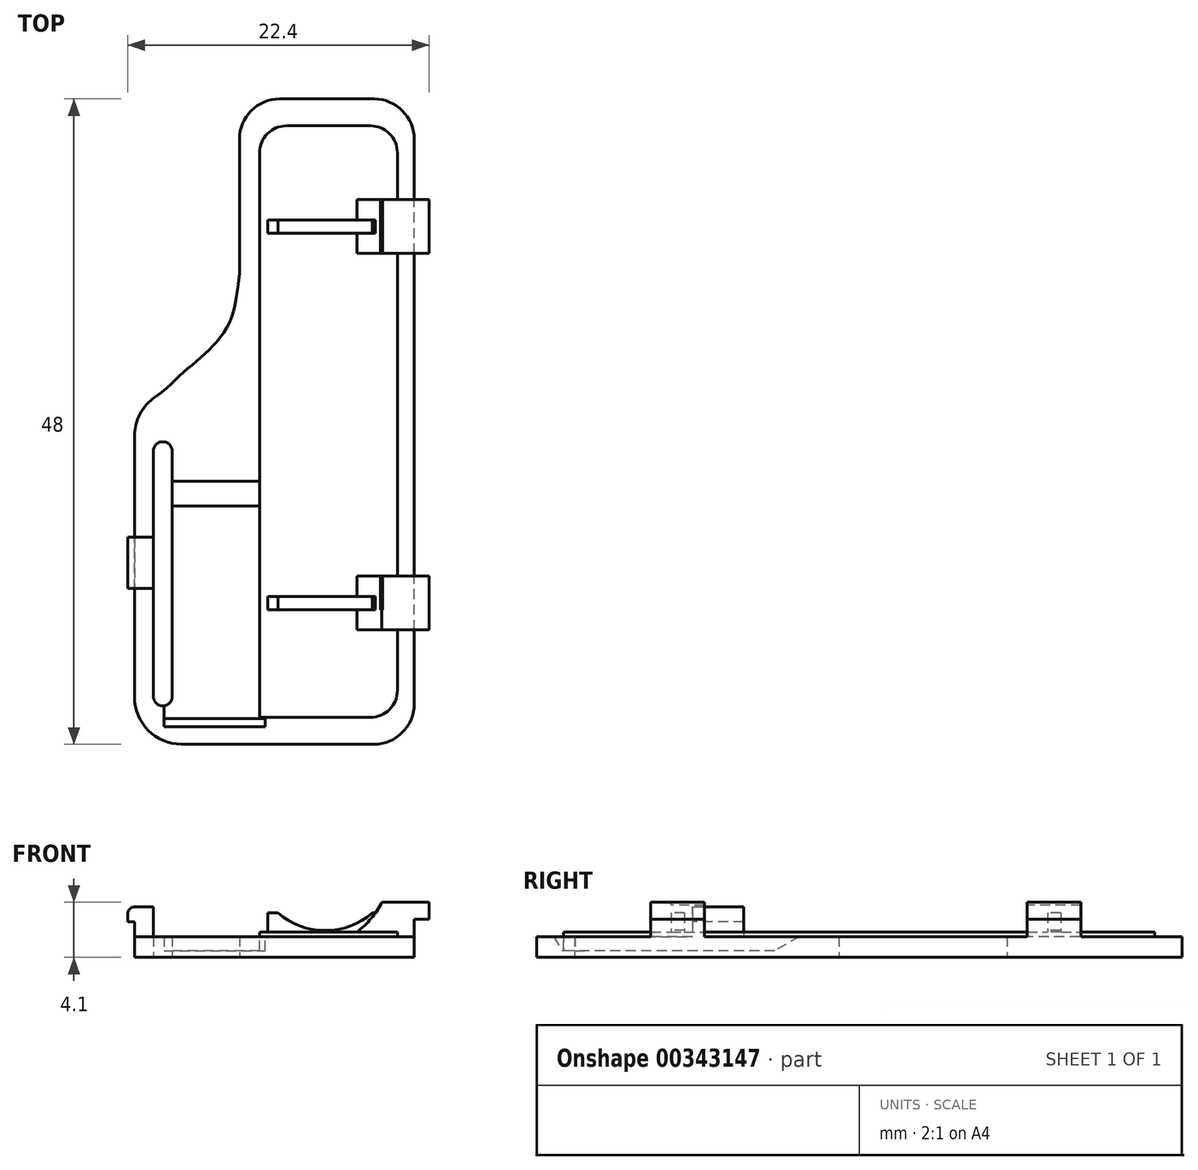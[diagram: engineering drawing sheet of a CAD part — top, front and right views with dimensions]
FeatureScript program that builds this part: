
annotation { "Feature Type Name" : "Feature", "Feature Type Description" : "" }
export const myFeature = defineFeature(function(context is Context, id is Id, definition is map)
    precondition{}
    {
        {
            var Q0;
            Q0=qCreatedBy(makeId("Top.planeOp"),FACE);
            var sketch = newSketch(context, id + "F0", { "sketchPlane" : qUnion([Q0])});
            skLineSegment(sketch, "E0.bottom", {"start": v(1.82, -24.92) * mm, "end": v(-12.48, -24.92) * mm});
            skLineSegment(sketch, "E0.top", {"start": v(1.82, 23.08) * mm, "end": v(-5.18, 23.08) * mm});
            skLineSegment(sketch, "E0.left", {"start": v(4.82, -21.92) * mm, "end": v(4.82, 20.08) * mm});
            skLineSegment(sketch, "E0.right", {"start": v(-15.98, -21.42) * mm, "end": v(-15.98, -2) * mm});
            skLineSegment(sketch, "E1", {"start": v(-8.18, 20.08) * mm, "end": v(-8.18, 10.08) * mm});
            skPoint(sketch, "E2.visualSharp", {"position": v(4.82, 23.08) * mm});
            skArc(sketch, "E2.filletArc", {"start": v(4.82, 20.08) * mm, "mid": v(3.94, 22.2) * mm, "end": v(1.82, 23.08) * mm});
            skPoint(sketch, "E3.visualSharp", {"position": v(4.82, -24.92) * mm});
            skArc(sketch, "E3.filletArc", {"start": v(1.82, -24.92) * mm, "mid": v(3.94, -24.04) * mm, "end": v(4.82, -21.92) * mm});
            skPoint(sketch, "E4.visualSharp", {"position": v(-15.98, -24.92) * mm});
            skArc(sketch, "E4.filletArc", {"start": v(-15.98, -21.42) * mm, "mid": v(-14.95, -23.9) * mm, "end": v(-12.48, -24.92) * mm});
            skPoint(sketch, "E5.visualSharp", {"position": v(-8.18, 23.08) * mm});
            skArc(sketch, "E5.filletArc", {"start": v(-5.18, 23.08) * mm, "mid": v(-7.3, 22.2) * mm, "end": v(-8.18, 20.08) * mm});
            skFitSpline(sketch, "E6", {"points": [v(-8.18, 10.08) * mm, v(-9.53, 5.44) * mm, v(-11.08, 3.82) * mm, v(-12.77, 2.37) * mm, v(-15.98, 0.08) * mm], "startDerivative": vector(-2.45, -27.24) * mm, "endDerivative": vector(-20.78, -9.12) * mm});
            skArc(sketch, "E7.filletArc", {"start": v(-14.43, 0.92) * mm, "mid": v(-15.57, -0.34) * mm, "end": v(-15.98, -2) * mm});
            skLineSegment(sketch, "E8.bottom", {"start": v(-13.88, -2.42) * mm, "end": v(-13.88, -2.42) * mm});
            skLineSegment(sketch, "E8.top", {"start": v(-13.88, -22.07) * mm, "end": v(-13.88, -22.07) * mm});
            skLineSegment(sketch, "E8.left", {"start": v(-14.58, -3.12) * mm, "end": v(-14.58, -21.37) * mm});
            skLineSegment(sketch, "E8.right", {"start": v(-13.18, -3.12) * mm, "end": v(-13.18, -21.37) * mm});
            skPoint(sketch, "E9.visualSharp", {"position": v(-14.58, -2.42) * mm});
            skArc(sketch, "E9.filletArc", {"start": v(-13.88, -2.42) * mm, "mid": v(-14.37, -2.62) * mm, "end": v(-14.58, -3.12) * mm});
            skPoint(sketch, "E10.visualSharp", {"position": v(-13.18, -2.42) * mm});
            skArc(sketch, "E10.filletArc", {"start": v(-13.18, -3.12) * mm, "mid": v(-13.38, -2.62) * mm, "end": v(-13.88, -2.42) * mm});
            skPoint(sketch, "E11.visualSharp", {"position": v(-14.58, -22.07) * mm});
            skArc(sketch, "E11.filletArc", {"start": v(-14.58, -21.37) * mm, "mid": v(-14.37, -21.86) * mm, "end": v(-13.88, -22.07) * mm});
            skPoint(sketch, "E12.visualSharp", {"position": v(-13.18, -22.07) * mm});
            skArc(sketch, "E12.filletArc", {"start": v(-13.88, -22.07) * mm, "mid": v(-13.38, -21.86) * mm, "end": v(-13.18, -21.37) * mm});
            skSolve(sketch);
        }
        {
            var Q0;
            Q0=makeQuery(id+"F0.imprint","IMPRINT",FACE,{"disambiguationData":[TD([[makeQuery(id+"F0.imprint","IMPRINT",EDGE,{"derivedFrom":sQuery(id+"F0.wireOp",EDGE,"E0.bottom")}),-1.0]])]});
            extrude(context, id + "F1", {"entities" : qUnion([Q0]), "depth" : 1.55 * mm});
        }
        {
            var Q0;
            Q0=makeQuery(id+"F1.opExtrude","CAP_FACE",FACE,{"disambiguationData":[OSD([sQuery(id+"F0.wireOp",EDGE,"E0.bottom"),sQuery(id+"F0.wireOp",EDGE,"E0.top"),sQuery(id+"F0.wireOp",EDGE,"E0.left"),sQuery(id+"F0.wireOp",EDGE,"E0.right"),sQuery(id+"F0.wireOp",EDGE,"E1"),sQuery(id+"F0.wireOp",EDGE,"E2.filletArc"),sQuery(id+"F0.wireOp",EDGE,"E3.filletArc"),sQuery(id+"F0.wireOp",EDGE,"E4.filletArc"),sQuery(id+"F0.wireOp",EDGE,"E5.filletArc"),sQuery(id+"F0.wireOp",EDGE,"E6"),sQuery(id+"F0.wireOp",EDGE,"E7.filletArc"),sQuery(id+"F0.wireOp",EDGE,"E8.left"),sQuery(id+"F0.wireOp",EDGE,"E8.right"),sQuery(id+"F0.wireOp",EDGE,"E9.filletArc"),sQuery(id+"F0.wireOp",EDGE,"E10.filletArc"),sQuery(id+"F0.wireOp",EDGE,"E11.filletArc"),sQuery(id+"F0.wireOp",EDGE,"E12.filletArc")])],"isStart":false});
            var sketch = newSketch(context, id + "F2", { "sketchPlane" : qUnion([Q0])});
            skLineSegment(sketch, "E13.bottom", {"start": v(-4.68, 21.08) * mm, "end": v(1.57, 21.08) * mm});
            skLineSegment(sketch, "E13.top", {"start": v(-6.68, -22.92) * mm, "end": v(1.57, -22.92) * mm});
            skLineSegment(sketch, "E13.left", {"start": v(-6.68, 19.08) * mm, "end": v(-6.68, -22.92) * mm});
            skLineSegment(sketch, "E13.right", {"start": v(3.57, 19.08) * mm, "end": v(3.57, -20.92) * mm});
            skPoint(sketch, "E14.visualSharp", {"position": v(-6.68, 21.08) * mm});
            skArc(sketch, "E14.filletArc", {"start": v(-4.68, 21.08) * mm, "mid": v(-6.1, 20.5) * mm, "end": v(-6.68, 19.08) * mm});
            skPoint(sketch, "E15.visualSharp", {"position": v(3.57, 21.08) * mm});
            skArc(sketch, "E15.filletArc", {"start": v(3.57, 19.08) * mm, "mid": v(2.98, 20.5) * mm, "end": v(1.57, 21.08) * mm});
            skPoint(sketch, "E16.visualSharp", {"position": v(3.57, -22.92) * mm});
            skArc(sketch, "E16.filletArc", {"start": v(1.57, -22.92) * mm, "mid": v(2.98, -22.33) * mm, "end": v(3.57, -20.92) * mm});
            skSolve(sketch);
        }
        {
            var Q0;
            Q0=makeQuery(id+"F2.imprint","IMPRINT",FACE,{"disambiguationData":[TD([[makeQuery(id+"F2.imprint","IMPRINT",EDGE,{"derivedFrom":sQuery(id+"F2.wireOp",EDGE,"E13.bottom")}),-1.0]])]});
            extrude(context, id + "F3", {"entities" : qUnion([Q0]), "operationType" : NewBodyOperationType.ADD, "depth" : (2 - 1.65) * mm});
        }
        {
            var Q0;
            Q0=makeQuery(id+"F3.opExtrude","CAP_FACE",FACE,{"disambiguationData":[OSD([sQuery(id+"F2.wireOp",EDGE,"E13.bottom"),sQuery(id+"F2.wireOp",EDGE,"E13.top"),sQuery(id+"F2.wireOp",EDGE,"E13.left"),sQuery(id+"F2.wireOp",EDGE,"E13.right"),sQuery(id+"F2.wireOp",EDGE,"E14.filletArc"),sQuery(id+"F2.wireOp",EDGE,"E15.filletArc"),sQuery(id+"F2.wireOp",EDGE,"E16.filletArc")])],"isStart":false});
            var sketch = newSketch(context, id + "F4", { "sketchPlane" : qUnion([Q0])});
            skLineSegment(sketch, "E17", {"start": v(-6.08, -14.92) * mm, "end": v(2.57, -14.92) * mm});
            skLineSegment(sketch, "E18", {"start": v(-6.08, -14.92) * mm, "end": v(-6.08, -13.92) * mm});
            skLineSegment(sketch, "E19", {"start": v(-6.08, -13.92) * mm, "end": v(2.57, -13.92) * mm});
            skLineSegment(sketch, "E20", {"start": v(2.57, -13.92) * mm, "end": v(2.57, -14.92) * mm});
            skLineSegment(sketch, "E21", {"start": v(-5.63, -0.42) * mm, "end": v(1.6, -0.42) * mm});
            skLineSegment(sketch, "E22.MirrorCS", {"start": v(-6.08, 13.08) * mm, "end": v(2.57, 13.08) * mm});
            skLineSegment(sketch, "E23.MirrorCS", {"start": v(-6.08, 14.08) * mm, "end": v(2.57, 14.08) * mm});
            skLineSegment(sketch, "E24.MirrorCS", {"start": v(-6.08, 14.08) * mm, "end": v(-6.08, 13.08) * mm});
            skLineSegment(sketch, "E25.MirrorCS", {"start": v(2.57, 13.08) * mm, "end": v(2.57, 14.08) * mm});
            skSolve(sketch);
        }
        {
            var Q0;
            Q0=makeQuery(id+"F4.imprint","IMPRINT",FACE,{"disambiguationData":[TD([[makeQuery(id+"F4.imprint","IMPRINT",EDGE,{"derivedFrom":sQuery(id+"F4.wireOp",EDGE,"E24.MirrorCS")}),1.0]])]});
            var Q1;
            Q1=makeQuery(id+"F4.imprint","IMPRINT",FACE,{"disambiguationData":[TD([[makeQuery(id+"F4.imprint","IMPRINT",EDGE,{"derivedFrom":sQuery(id+"F4.wireOp",EDGE,"E17")}),1.0]])]});
            extrude(context, id + "F5", {"entities" : qUnion([Q0, Q1]), "operationType" : NewBodyOperationType.ADD, "depth" : (3.4 - 2.1) * mm});
        }
        {
            var Q0;
            Q0=makeQuery(id+"F5.opExtrude","SWEPT_FACE",FACE,{"disambiguationData":[OSD([sQuery(id+"F4.wireOp",EDGE,"E17")])]});
            var sketch = newSketch(context, id + "F6", { "sketchPlane" : qUnion([Q0])});
            skLineSegment(sketch, "E26", {"start": v(-5.2, 3.2) * mm, "end": v(1.6, 3.2) * mm});
            skLineSegment(sketch, "E27", {"start": v(-6.08, 3.2) * mm, "end": v(-5.2, 3.2) * mm});
            skCircle(sketch, "E28", {"center": v(-1.8, 7.42) * mm, "radius": 5.42 * mm});
            skPoint(sketch, "E28.centerSnap0", {"position": v(-1.8, 3.2) * mm});
            skSolve(sketch);
        }
        {
            var Q0;
            Q0=makeQuery(id+"F1.opExtrude","CAP_FACE",FACE,{"disambiguationData":[OSD([sQuery(id+"F0.wireOp",EDGE,"E0.bottom"),sQuery(id+"F0.wireOp",EDGE,"E0.top"),sQuery(id+"F0.wireOp",EDGE,"E0.left"),sQuery(id+"F0.wireOp",EDGE,"E0.right"),sQuery(id+"F0.wireOp",EDGE,"E1"),sQuery(id+"F0.wireOp",EDGE,"E2.filletArc"),sQuery(id+"F0.wireOp",EDGE,"E3.filletArc"),sQuery(id+"F0.wireOp",EDGE,"E4.filletArc"),sQuery(id+"F0.wireOp",EDGE,"E5.filletArc"),sQuery(id+"F0.wireOp",EDGE,"E6"),sQuery(id+"F0.wireOp",EDGE,"E7.filletArc"),sQuery(id+"F0.wireOp",EDGE,"E8.left"),sQuery(id+"F0.wireOp",EDGE,"E8.right"),sQuery(id+"F0.wireOp",EDGE,"E9.filletArc"),sQuery(id+"F0.wireOp",EDGE,"E10.filletArc"),sQuery(id+"F0.wireOp",EDGE,"E11.filletArc"),sQuery(id+"F0.wireOp",EDGE,"E12.filletArc")])],"isStart":false});
            var sketch = newSketch(context, id + "F7", { "sketchPlane" : qUnion([Q0])});
            skLineSegment(sketch, "E29.0", {"start": v(9.82, -22.92) * mm, "end": v(9.82, 20.08) * mm, "construction": true});
            skLineSegment(sketch, "E30.bottom", {"start": v(4.82, -12.42) * mm, "end": v(0.57, -12.42) * mm, "construction": true});
            skLineSegment(sketch, "E30.top", {"start": v(4.82, -16.42) * mm, "end": v(0.57, -16.42) * mm, "construction": true});
            skLineSegment(sketch, "E30.left", {"start": v(4.82, -12.42) * mm, "end": v(4.82, -16.42) * mm, "construction": true});
            skLineSegment(sketch, "E30.right", {"start": v(0.57, -12.42) * mm, "end": v(0.57, -16.42) * mm, "construction": true});
            skLineSegment(sketch, "E31", {"start": v(-2, -0.42) * mm, "end": v(2.13, -0.42) * mm});
            skLineSegment(sketch, "E32.MirrorCS", {"start": v(4.82, 11.58) * mm, "end": v(0.57, 11.58) * mm, "construction": true});
            skLineSegment(sketch, "E33.MirrorCS", {"start": v(4.82, 11.58) * mm, "end": v(4.82, 15.58) * mm, "construction": true});
            skLineSegment(sketch, "E34.MirrorCS", {"start": v(4.82, 15.58) * mm, "end": v(0.57, 15.58) * mm, "construction": true});
            skLineSegment(sketch, "E35.MirrorCS", {"start": v(0.57, 11.58) * mm, "end": v(0.57, 15.58) * mm, "construction": true});
            skLineSegment(sketch, "E36.bottom", {"start": v(0.57, -12.42) * mm, "end": v(4.82, -12.42) * mm});
            skLineSegment(sketch, "E36.top", {"start": v(0.57, -16.42) * mm, "end": v(4.82, -16.42) * mm});
            skLineSegment(sketch, "E36.left", {"start": v(0.57, -12.42) * mm, "end": v(0.57, -16.42) * mm});
            skLineSegment(sketch, "E36.right", {"start": v(4.82, -12.42) * mm, "end": v(4.82, -16.42) * mm});
            skLineSegment(sketch, "E37.bottom", {"start": v(0.57, 15.58) * mm, "end": v(4.82, 15.58) * mm});
            skLineSegment(sketch, "E37.top", {"start": v(0.57, 11.58) * mm, "end": v(4.82, 11.58) * mm});
            skLineSegment(sketch, "E37.left", {"start": v(0.57, 15.58) * mm, "end": v(0.57, 11.58) * mm});
            skLineSegment(sketch, "E37.right", {"start": v(4.82, 15.58) * mm, "end": v(4.82, 11.58) * mm});
            skSolve(sketch);
        }
        {
            var Q0;
            Q0 = qSketchRegion(id + "F7", true);
            extrude(context, id + "F8", {"entities" : qUnion([Q0]), "operationType" : NewBodyOperationType.ADD, "depth" : (4.15 - 1.6) * mm});
        }
        {
            var Q0;
            Q0=makeQuery(id+"F8.opExtrude","SWEPT_FACE",FACE,{"disambiguationData":[OSD([sQuery(id+"F7.wireOp",EDGE,"E36.top")])]});
            var sketch = newSketch(context, id + "F9", { "sketchPlane" : qUnion([Q0])});
            skCircle(sketch, "E38", {"center": v(-3.26, 7) * mm, "radius": 6.38 * mm});
            skPoint(sketch, "E39", {"position": v(2.42, 4.1) * mm});
            skLineSegment(sketch, "E40", {"start": v(0.57, 1.9) * mm, "end": v(0.57, 4.1) * mm});
            skLineSegment(sketch, "E41", {"start": v(0.57, 4.1) * mm, "end": v(2.42, 4.1) * mm});
            skSolve(sketch);
        }
        {
            var Q0;
            {var subQ0=sQuery(id+"F9.wireOp",EDGE,"E40");Q0=makeQuery(id+"F9.imprint","IMPRINT",FACE,{"disambiguationData":[TD([[makeQuery(id+"F9.imprint","IMPRINT",EDGE,{"derivedFrom":subQ0}),1.0]])]});}
            extrude(context, id + "F10", {"entities" : qUnion([Q0]), "operationType" : NewBodyOperationType.REMOVE, "endBound" : BoundingType.THROUGH_ALL, "oppositeDirection" : true, "depth" : 25 * mm});
        }
        {
            var Q0;
            Q0=makeQuery(id+"F8.boolean.opBoolean","MERGE",FACE,{"derivedFrom":[makeQuery(id+"F1.opExtrude","SWEPT_FACE",FACE,{"disambiguationData":[OSD([sQuery(id+"F0.wireOp",EDGE,"E0.left")])]}),makeQuery(id+"F8.opExtrude","SWEPT_FACE",FACE,{"disambiguationData":[OSD([sQuery(id+"F7.wireOp",EDGE,"E36.right")])]}),makeQuery(id+"F8.opExtrude","SWEPT_FACE",FACE,{"disambiguationData":[OSD([sQuery(id+"F7.wireOp",EDGE,"E37.right")])]})]});
            var sketch = newSketch(context, id + "F11", { "sketchPlane" : qUnion([Q0])});
            skLineSegment(sketch, "E42.bottom", {"start": v(11.58, 4.1) * mm, "end": v(15.58, 4.1) * mm});
            skLineSegment(sketch, "E42.top", {"start": v(11.58, 2.83) * mm, "end": v(15.58, 2.83) * mm});
            skLineSegment(sketch, "E42.left", {"start": v(11.58, 4.1) * mm, "end": v(11.58, 2.83) * mm});
            skLineSegment(sketch, "E42.right", {"start": v(15.58, 4.1) * mm, "end": v(15.58, 2.83) * mm});
            skLineSegment(sketch, "E43.bottom", {"start": v(-16.42, 4.1) * mm, "end": v(-12.42, 4.1) * mm});
            skLineSegment(sketch, "E43.top", {"start": v(-16.42, 2.83) * mm, "end": v(-12.42, 2.83) * mm});
            skLineSegment(sketch, "E43.left", {"start": v(-16.42, 4.1) * mm, "end": v(-16.42, 2.83) * mm});
            skLineSegment(sketch, "E43.right", {"start": v(-12.42, 4.1) * mm, "end": v(-12.42, 2.83) * mm});
            skLineSegment(sketch, "E44", {"start": v(11.58, 1.55) * mm, "end": v(11.58, 2.83) * mm});
            skLineSegment(sketch, "E45", {"start": v(-12.42, 1.55) * mm, "end": v(-12.42, 2.83) * mm});
            skSolve(sketch);
        }
        {
            var Q0;
            Q0=makeQuery(id+"F11.imprint","IMPRINT",FACE,{"disambiguationData":[TD([[makeQuery(id+"F11.imprint","IMPRINT",EDGE,{"derivedFrom":sQuery(id+"F11.wireOp",EDGE,"E43.bottom")}),-1.0]])]});
            var Q1;
            Q1=makeQuery(id+"F11.imprint","IMPRINT",FACE,{"disambiguationData":[TD([[makeQuery(id+"F11.imprint","IMPRINT",EDGE,{"derivedFrom":sQuery(id+"F11.wireOp",EDGE,"E42.bottom")}),-1.0]])]});
            extrude(context, id + "F12", {"entities" : qUnion([Q0, Q1]), "operationType" : NewBodyOperationType.ADD, "depth" : 1.1 * mm});
        }
        {
            var Q0;
            Q0=makeQuery(id+"F3.opExtrude","CAP_FACE",FACE,{"disambiguationData":[OSD([sQuery(id+"F2.wireOp",EDGE,"E13.bottom"),sQuery(id+"F2.wireOp",EDGE,"E13.top"),sQuery(id+"F2.wireOp",EDGE,"E13.left"),sQuery(id+"F2.wireOp",EDGE,"E13.right"),sQuery(id+"F2.wireOp",EDGE,"E14.filletArc"),sQuery(id+"F2.wireOp",EDGE,"E15.filletArc"),sQuery(id+"F2.wireOp",EDGE,"E16.filletArc")])],"isStart":false});
            var sketch = newSketch(context, id + "F13", { "sketchPlane" : qUnion([Q0])});
            skLineSegment(sketch, "E46", {"start": v(-6.08, -14.92) * mm, "end": v(2.57, -14.92) * mm});
            skLineSegment(sketch, "E47", {"start": v(-6.08, -14.92) * mm, "end": v(-6.08, -13.92) * mm});
            skLineSegment(sketch, "E48", {"start": v(-6.08, -13.92) * mm, "end": v(2.57, -13.92) * mm});
            skLineSegment(sketch, "E49", {"start": v(2.57, -13.92) * mm, "end": v(2.57, -14.92) * mm});
            skLineSegment(sketch, "E50", {"start": v(-3.47, -0.42) * mm, "end": v(3.75, -0.42) * mm});
            skLineSegment(sketch, "E51.MirrorCS", {"start": v(-6.08, 13.08) * mm, "end": v(2.57, 13.08) * mm});
            skLineSegment(sketch, "E52.MirrorCS", {"start": v(-6.08, 14.08) * mm, "end": v(2.57, 14.08) * mm});
            skLineSegment(sketch, "E53.MirrorCS", {"start": v(-6.08, 14.08) * mm, "end": v(-6.08, 13.08) * mm});
            skLineSegment(sketch, "E54.MirrorCS", {"start": v(2.57, 13.08) * mm, "end": v(2.57, 14.08) * mm});
            skLineSegment(sketch, "E55.right", {"start": v(2.57, 14.08) * mm, "end": v(2.57, 13.08) * mm});
            skLineSegment(sketch, "E56.left", {"start": v(-6.08, -13.92) * mm, "end": v(-6.08, -14.92) * mm});
            skSolve(sketch);
        }
        {
            var Q0;
            Q0 = qSketchRegion(id + "F13", true);
            extrude(context, id + "F14", {"entities" : qUnion([Q0]), "operationType" : NewBodyOperationType.ADD, "depth" : 1.4 * mm});
        }
        {
            var Q0;
            {var subQ0=sQuery(id+"F6.wireOp",EDGE,"E26");Q0=makeQuery(id+"F6.imprint","IMPRINT",FACE,{"disambiguationData":[TD([[makeQuery(id+"F6.imprint","IMPRINT",EDGE,{"derivedFrom":subQ0}),-1.0]])]});}
            var Q1;
            {var subQ0=sQuery(id+"F6.wireOp",EDGE,"E26");Q1=makeQuery(id+"F6.imprint","IMPRINT",FACE,{"disambiguationData":[TD([[makeQuery(id+"F6.imprint","IMPRINT",EDGE,{"derivedFrom":subQ0}),1.0]])]});}
            extrude(context, id + "F15", {"entities" : qUnion([Q0, Q1]), "operationType" : NewBodyOperationType.REMOVE, "endBound" : BoundingType.THROUGH_ALL, "oppositeDirection" : true, "depth" : 25 * mm});
        }
        {
            var Q0;
            Q0=makeQuery(id+"F3.opExtrude","CAP_FACE",FACE,{"disambiguationData":[OSD([sQuery(id+"F2.wireOp",EDGE,"E13.bottom"),sQuery(id+"F2.wireOp",EDGE,"E13.top"),sQuery(id+"F2.wireOp",EDGE,"E13.left"),sQuery(id+"F2.wireOp",EDGE,"E13.right"),sQuery(id+"F2.wireOp",EDGE,"E14.filletArc"),sQuery(id+"F2.wireOp",EDGE,"E15.filletArc"),sQuery(id+"F2.wireOp",EDGE,"E16.filletArc")])],"isStart":false});
            var sketch = newSketch(context, id + "F16", { "sketchPlane" : qUnion([Q0])});
            skLineSegment(sketch, "E57.0", {"start": v(-13.18, -3.12) * mm, "end": v(-13.18, -21.37) * mm});
            skLineSegment(sketch, "E58.0", {"start": v(-6.68, 19.08) * mm, "end": v(-6.68, -22.92) * mm});
            skLineSegment(sketch, "E59.bottom", {"start": v(-13.78, -5.28) * mm, "end": v(-6.26, -5.28) * mm});
            skLineSegment(sketch, "E59.top", {"start": v(-13.78, -23.72) * mm, "end": v(-6.26, -23.72) * mm});
            skLineSegment(sketch, "E59.left", {"start": v(-13.78, -5.28) * mm, "end": v(-13.78, -23.72) * mm});
            skLineSegment(sketch, "E59.right", {"start": v(-6.26, -5.28) * mm, "end": v(-6.26, -23.72) * mm});
            skLineSegment(sketch, "E60.0", {"start": v(1.82, -24.92) * mm, "end": v(-12.48, -24.92) * mm});
            skSolve(sketch);
        }
        {
            var Q0;
            {var subQ5=sQuery(id+"F16.wireOp",EDGE,"E59.left");Q0=makeQuery(id+"F16.imprint","IMPRINT",FACE,{"disambiguationData":[TD([[makeQuery(id+"F16.imprint","IMPRINT",EDGE,{"derivedFrom":subQ5}),1.0]])]});}
            extrude(context, id + "F17", {"entities" : qUnion([Q0]), "operationType" : NewBodyOperationType.REMOVE, "oppositeDirection" : true, "depth" : 1.4 * mm});
        }
        {
            var Q0;
            Q0=makeQuery(id+"F17.boolean.opBoolean","COPY",EDGE,{"derivedFrom":makeQuery(id+"F17.opExtrude","CAP_EDGE",EDGE,{"disambiguationData":[OSD([sQuery(id+"F16.wireOp",EDGE,"E59.bottom")])],"isStart":false})});
            chamfer(context, id + "F18", {"entities" : qUnion([Q0]), "chamferType" : ChamferType.OFFSET_ANGLE, "width" : 1.1 * mm, "oppositeDirection" : false, "angle" : 60 * degree, "tangentPropagation" : true});
        }
        {
            var Q0;
            Q0=makeQuery(id+"F17.boolean.opBoolean","COPY",EDGE,{"derivedFrom":makeQuery(id+"F17.opExtrude","CAP_EDGE",EDGE,{"disambiguationData":[OSD([sQuery(id+"F16.wireOp",EDGE,"E59.top")])],"isStart":false})});
            chamfer(context, id + "F19", {"entities" : qUnion([Q0]), "chamferType" : ChamferType.OFFSET_ANGLE, "width" : 0.7 * mm, "oppositeDirection" : false, "angle" : 60 * degree, "tangentPropagation" : true});
        }
        {
            var Q0;
            {var subQ0=sQuery(id+"F0.wireOp",EDGE,"E12.filletArc");var subQ1=sQuery(id+"F0.wireOp",EDGE,"E11.filletArc");var subQ2=sQuery(id+"F0.wireOp",EDGE,"E10.filletArc");var subQ3=sQuery(id+"F0.wireOp",EDGE,"E9.filletArc");var subQ4=sQuery(id+"F0.wireOp",EDGE,"E8.right");var subQ5=sQuery(id+"F0.wireOp",EDGE,"E8.left");var subQ6=sQuery(id+"F0.wireOp",EDGE,"E7.filletArc");var subQ7=sQuery(id+"F0.wireOp",EDGE,"E0.left");var subQ8=sQuery(id+"F0.wireOp",EDGE,"E0.top");var subQ9=sQuery(id+"F0.wireOp",EDGE,"E0.right");var subQ10=sQuery(id+"F0.wireOp",EDGE,"E0.bottom");var subQ11=sQuery(id+"F0.wireOp",EDGE,"E6");var subQ12=sQuery(id+"F0.wireOp",EDGE,"E1");var subQ13=sQuery(id+"F0.wireOp",EDGE,"E2.filletArc");var subQ14=sQuery(id+"F0.wireOp",EDGE,"E3.filletArc");var subQ15=sQuery(id+"F0.wireOp",EDGE,"E4.filletArc");var subQ16=sQuery(id+"F0.wireOp",EDGE,"E5.filletArc");Q0=makeQuery(id+"F8.boolean.opBoolean","SPLIT",FACE,{"disambiguationData":[TD([makeQuery(id+"F1.opExtrude","SWEPT_FACE",FACE,{"disambiguationData":[OSD([subQ10])]})])],"derivedFrom":makeQuery(id+"F1.opExtrude","CAP_FACE",FACE,{"disambiguationData":[OSD([subQ10,subQ8,subQ7,subQ9,subQ12,subQ13,subQ14,subQ15,subQ16,subQ11,subQ6,subQ5,subQ4,subQ3,subQ2,subQ1,subQ0])],"isStart":false})});}
            var sketch = newSketch(context, id + "F20", { "sketchPlane" : qUnion([Q0])});
            skLineSegment(sketch, "E61.bottom", {"start": v(-15.98, -8.92) * mm, "end": v(-20.32, -8.92) * mm});
            skLineSegment(sketch, "E61.top", {"start": v(-15.98, -13.92) * mm, "end": v(-20.32, -13.92) * mm});
            skLineSegment(sketch, "E61.left", {"start": v(-15.98, -8.92) * mm, "end": v(-15.98, -13.92) * mm});
            skLineSegment(sketch, "E61.right", {"start": v(-20.32, -8.92) * mm, "end": v(-20.32, -13.92) * mm});
            skLineSegment(sketch, "E62.bottom", {"start": v(-15.98, -9.52) * mm, "end": v(-16.98, -9.52) * mm});
            skLineSegment(sketch, "E62.top", {"start": v(-15.98, -13.32) * mm, "end": v(-16.98, -13.32) * mm});
            skLineSegment(sketch, "E62.left", {"start": v(-15.98, -9.52) * mm, "end": v(-15.98, -13.32) * mm});
            skLineSegment(sketch, "E62.right", {"start": v(-16.98, -9.52) * mm, "end": v(-16.98, -13.32) * mm});
            skLineSegment(sketch, "E63.bottom", {"start": v(-15.98, -9.52) * mm, "end": v(-14.58, -9.52) * mm});
            skLineSegment(sketch, "E63.top", {"start": v(-15.98, -13.32) * mm, "end": v(-14.58, -13.32) * mm});
            skLineSegment(sketch, "E63.right", {"start": v(-14.58, -9.52) * mm, "end": v(-14.58, -13.32) * mm});
            skSolve(sketch);
        }
        {
            var Q0;
            Q0=makeQuery(id+"F20.imprint","IMPRINT",FACE,{"disambiguationData":[TD([[makeQuery(id+"F20.imprint","IMPRINT",EDGE,{"derivedFrom":sQuery(id+"F20.wireOp",EDGE,"E63.bottom")}),-1.0]])]});
            extrude(context, id + "F21", {"entities" : qUnion([Q0]), "operationType" : NewBodyOperationType.ADD, "depth" : 2.2 * mm});
        }
        {
            var Q0;
            Q0=makeQuery(id+"F21.boolean.opBoolean","MERGE",FACE,{"derivedFrom":[makeQuery(id+"F1.opExtrude","SWEPT_FACE",FACE,{"disambiguationData":[OSD([sQuery(id+"F0.wireOp",EDGE,"E0.right")])]}),makeQuery(id+"F21.opExtrude","SWEPT_FACE",FACE,{"disambiguationData":[OSD([sQuery(id+"F20.wireOp",EDGE,"E62.left")])]})]});
            var sketch = newSketch(context, id + "F22", { "sketchPlane" : qUnion([Q0])});
            skLineSegment(sketch, "E64.bottom", {"start": v(9.52, 3.75) * mm, "end": v(13.32, 3.75) * mm});
            skLineSegment(sketch, "E64.top", {"start": v(9.52, 2.65) * mm, "end": v(13.32, 2.65) * mm});
            skLineSegment(sketch, "E64.left", {"start": v(9.52, 3.75) * mm, "end": v(9.52, 2.65) * mm});
            skLineSegment(sketch, "E64.right", {"start": v(13.32, 3.75) * mm, "end": v(13.32, 2.65) * mm});
            skSolve(sketch);
        }
        {
            var Q0;
            Q0=makeQuery(id+"F22.imprint","IMPRINT",FACE,{"disambiguationData":[TD([[makeQuery(id+"F22.imprint","IMPRINT",EDGE,{"derivedFrom":sQuery(id+"F22.wireOp",EDGE,"E64.bottom")}),1.0]])]});
            extrude(context, id + "F23", {"entities" : qUnion([Q0]), "operationType" : NewBodyOperationType.ADD, "depth" : .5 * mm});
        }
        {
            var Q0;
            Q0=makeQuery(id+"F21.opExtrude","CAP_EDGE",EDGE,{"disambiguationData":[OSD([sQuery(id+"F20.wireOp",EDGE,"E63.top")])],"isStart":true});
            var Q1;
            Q1=makeQuery(id+"F21.opExtrude","CAP_EDGE",EDGE,{"disambiguationData":[OSD([sQuery(id+"F20.wireOp",EDGE,"E63.bottom")])],"isStart":true});
            var Q2;
            Q2=makeQuery(id+"F23.opExtrude","CAP_EDGE",EDGE,{"disambiguationData":[OSD([sQuery(id+"F22.wireOp",EDGE,"E64.bottom")])],"isStart":false});
            fillet(context, id + "F24", {"entities" : qUnion([Q0, Q1, Q2]), "radius" : .5 * mm, "tangentPropagation" : true, "allowEdgeOverflow" : false});
        }
    });
